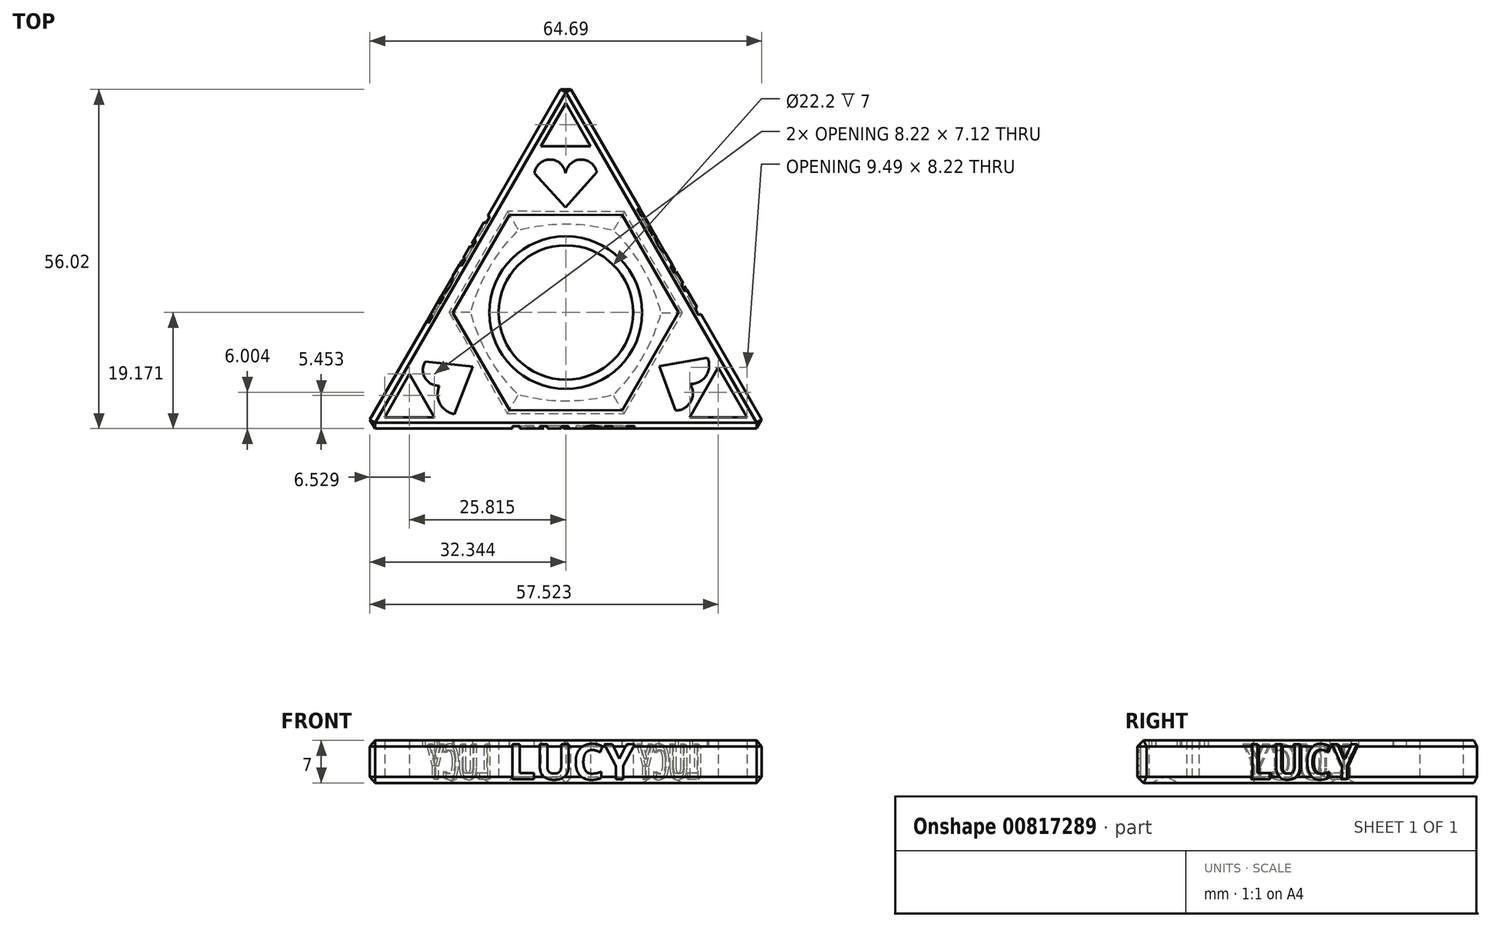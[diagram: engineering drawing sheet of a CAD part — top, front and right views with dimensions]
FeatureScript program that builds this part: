
annotation { "Feature Type Name" : "Feature", "Feature Type Description" : "" }
export const myFeature = defineFeature(function(context is Context, id is Id, definition is map)
    precondition{}
    {
        {
            var Q0;
            Q0=qCreatedBy(makeId("Top.planeOp"),FACE);
            var sketch = newSketch(context, id + "F0", { "sketchPlane" : qUnion([Q0])});
            skLineSegment(sketch, "E0.top", {"start": v(-48.66, -50.6) * mm, "end": v(17.76, -50.6) * mm});
            skLineSegment(sketch, "E1", {"start": v(-48.66, -50.6) * mm, "end": v(-15.45, 6.92) * mm});
            skLineSegment(sketch, "E2", {"start": v(-15.45, 6.92) * mm, "end": v(17.76, -50.6) * mm});
            skCircle(sketch, "E3", {"center": v(-15.45, -31.43) * mm, "radius": 11.1 * mm});
            skPoint(sketch, "E4.start.orphan", {"position": v(-32.05, -21.84) * mm});
            skPoint(sketch, "E5.trimOffspring.end.orphan", {"position": v(-15.45, -50.6) * mm});
            skPoint(sketch, "E6.trimOffspring.end.orphan", {"position": v(0, -21.31) * mm});
            skLineSegment(sketch, "E7.0", {"start": v(-45.37, -48.7) * mm, "end": v(-41.26, -41.59) * mm});
            skLineSegment(sketch, "E8.0", {"start": v(-15.45, 3.12) * mm, "end": v(-11.34, -4) * mm});
            skLineSegment(sketch, "E9.0", {"start": v(-45.37, -48.7) * mm, "end": v(-37.15, -48.7) * mm});
            skLineSegment(sketch, "E10", {"start": v(-37.15, -48.7) * mm, "end": v(-41.26, -41.59) * mm});
            skLineSegment(sketch, "E11", {"start": v(-15.45, -4) * mm, "end": v(-11.34, -4) * mm});
            skLineSegment(sketch, "E12", {"start": v(-15.45, -4) * mm, "end": v(-19.55, -4) * mm});
            skLineSegment(sketch, "E13", {"start": v(7.36, -44.6) * mm, "end": v(9.73, -40.49) * mm});
            skLineSegment(sketch, "E14", {"start": v(7.36, -44.6) * mm, "end": v(4.99, -48.7) * mm});
            skLineSegment(sketch, "E15.trimOffspring", {"start": v(4.99, -48.7) * mm, "end": v(14.48, -48.7) * mm});
            skLineSegment(sketch, "E16.trimOffspring", {"start": v(-19.55, -4) * mm, "end": v(-15.45, 3.12) * mm});
            skLineSegment(sketch, "E17.trimOffspring", {"start": v(9.73, -40.49) * mm, "end": v(14.48, -48.7) * mm});
            skSolve(sketch);
        }
        {
            var Q0;
            Q0=makeQuery(id+"F0.imprint","IMPRINT",FACE,{"disambiguationData":[TD([[makeQuery(id+"F0.imprint","IMPRINT",EDGE,{"derivedFrom":sQuery(id+"F0.wireOp",EDGE,"E0.top")}),1.0]])]});
            extrude(context, id + "F1", {"entities" : qUnion([Q0]), "depth" : 7 * mm, "offsetDistance" : 25 * mm});
        }
        {
            var Q0;
            Q0=makeQuery(id+"F1.opExtrude","SWEPT_FACE",FACE,{"disambiguationData":[OSD([sQuery(id+"F0.wireOp",EDGE,"E0.top")])]});
            var Q1;
            Q1=makeQuery(id+"F1.opExtrude","SWEPT_FACE",FACE,{"disambiguationData":[OSD([sQuery(id+"F0.wireOp",EDGE,"E2")])]});
            var Q2;
            Q2=makeQuery(id+"F1.opExtrude","SWEPT_FACE",FACE,{"disambiguationData":[OSD([sQuery(id+"F0.wireOp",EDGE,"E1")])]});
            chamfer(context, id + "F2", {"entities" : qUnion([Q0, Q1, Q2]), "width" : 1 * mm, "tangentPropagation" : true});
        }
        {
            var Q0;
            Q0=makeQuery(id+"F1.opExtrude","CAP_FACE",FACE,{"disambiguationData":[OSD([sQuery(id+"F0.wireOp",EDGE,"E0.top"),sQuery(id+"F0.wireOp",EDGE,"E1"),sQuery(id+"F0.wireOp",EDGE,"E2"),sQuery(id+"F0.wireOp",EDGE,"E3"),sQuery(id+"F0.wireOp",EDGE,"E7.0"),sQuery(id+"F0.wireOp",EDGE,"E8.0"),sQuery(id+"F0.wireOp",EDGE,"E9.0"),sQuery(id+"F0.wireOp",EDGE,"E10"),sQuery(id+"F0.wireOp",EDGE,"E11"),sQuery(id+"F0.wireOp",EDGE,"E12"),sQuery(id+"F0.wireOp",EDGE,"E13"),sQuery(id+"F0.wireOp",EDGE,"E14"),sQuery(id+"F0.wireOp",EDGE,"E15.trimOffspring"),sQuery(id+"F0.wireOp",EDGE,"E16.trimOffspring"),sQuery(id+"F0.wireOp",EDGE,"E17.trimOffspring")])],"isStart":false});
            var sketch = newSketch(context, id + "F3", { "sketchPlane" : qUnion([Q0])});
            skCircle(sketch, "E18.0", {"center": v(-15.45, -31.43) * mm, "radius": 12.6 * mm});
            skCircle(sketch, "E19.cCircle", {"center": v(-15.45, -31.43) * mm, "radius": 18.63 * mm, "construction": true});
            skLineSegment(sketch, "E19.0", {"start": v(-6.16, -15.28) * mm, "end": v(3.18, -31.4) * mm});
            skLineSegment(sketch, "E19.1", {"start": v(3.18, -31.4) * mm, "end": v(-6.1, -47.54) * mm});
            skLineSegment(sketch, "E19.2", {"start": v(-6.1, -47.54) * mm, "end": v(-24.73, -47.58) * mm});
            skLineSegment(sketch, "E19.3", {"start": v(-24.73, -47.58) * mm, "end": v(-34.08, -31.47) * mm});
            skLineSegment(sketch, "E19.4", {"start": v(-34.08, -31.47) * mm, "end": v(-24.8, -15.31) * mm});
            skLineSegment(sketch, "E19.5", {"start": v(-24.8, -15.31) * mm, "end": v(-6.16, -15.28) * mm});
            skSolve(sketch);
        }
        {
            var Q0;
            Q0=makeQuery(id+"F3.imprint","IMPRINT",FACE,{"disambiguationData":[TD([[makeQuery(id+"F3.imprint","IMPRINT",EDGE,{"derivedFrom":sQuery(id+"F3.wireOp",EDGE,"E18.0")}),-1.0]])]});
            extrude(context, id + "F4", {"entities" : qUnion([Q0]), "operationType" : NewBodyOperationType.REMOVE, "oppositeDirection" : true, "depth" : 1 * mm, "offsetDistance" : 25 * mm});
        }
        {
            var Q0;
            Q0=makeQuery(id+"F1.opExtrude","CAP_FACE",FACE,{"disambiguationData":[OSD([sQuery(id+"F0.wireOp",EDGE,"E0.top"),sQuery(id+"F0.wireOp",EDGE,"E1"),sQuery(id+"F0.wireOp",EDGE,"E2"),sQuery(id+"F0.wireOp",EDGE,"E3"),sQuery(id+"F0.wireOp",EDGE,"E7.0"),sQuery(id+"F0.wireOp",EDGE,"E8.0"),sQuery(id+"F0.wireOp",EDGE,"E9.0"),sQuery(id+"F0.wireOp",EDGE,"E10"),sQuery(id+"F0.wireOp",EDGE,"E11"),sQuery(id+"F0.wireOp",EDGE,"E12"),sQuery(id+"F0.wireOp",EDGE,"E13"),sQuery(id+"F0.wireOp",EDGE,"E14"),sQuery(id+"F0.wireOp",EDGE,"E15.trimOffspring"),sQuery(id+"F0.wireOp",EDGE,"E16.trimOffspring"),sQuery(id+"F0.wireOp",EDGE,"E17.trimOffspring")])],"isStart":true});
            var sketch = newSketch(context, id + "F5", { "sketchPlane" : qUnion([Q0])});
            skCircle(sketch, "E20.0", {"center": v(-15.45, 31.43) * mm, "radius": 12.6 * mm});
            skCircle(sketch, "E21.cCircle", {"center": v(-15.45, 31.43) * mm, "radius": 19.26 * mm, "construction": true});
            skLineSegment(sketch, "E21.0", {"start": v(-5.86, 48.14) * mm, "end": v(3.82, 31.48) * mm});
            skLineSegment(sketch, "E21.1", {"start": v(3.82, 31.48) * mm, "end": v(-5.77, 14.77) * mm});
            skLineSegment(sketch, "E21.2", {"start": v(-5.77, 14.77) * mm, "end": v(-25.04, 14.72) * mm});
            skLineSegment(sketch, "E21.3", {"start": v(-25.04, 14.72) * mm, "end": v(-34.7, 31.38) * mm});
            skLineSegment(sketch, "E21.4", {"start": v(-34.7, 31.38) * mm, "end": v(-25.12, 48.09) * mm});
            skLineSegment(sketch, "E21.5", {"start": v(-25.12, 48.09) * mm, "end": v(-5.86, 48.14) * mm});
            skSolve(sketch);
        }
        {
            var Q0;
            Q0=makeQuery(id+"F5.imprint","IMPRINT",FACE,{"disambiguationData":[TD([[makeQuery(id+"F5.imprint","IMPRINT",EDGE,{"derivedFrom":sQuery(id+"F5.wireOp",EDGE,"E20.0")}),-1.0]])]});
            extrude(context, id + "F6", {"entities" : qUnion([Q0]), "operationType" : NewBodyOperationType.REMOVE, "oppositeDirection" : true, "depth" : 1 * mm, "offsetDistance" : 25 * mm});
        }
        {
            var Q0;
            Q0=makeQuery(id+"F6.boolean.opBoolean","COPY",FACE,{"derivedFrom":makeQuery(id+"F6.opExtrude","CAP_FACE",FACE,{"disambiguationData":[OSD([sQuery(id+"F5.wireOp",EDGE,"E20.0"),sQuery(id+"F5.wireOp",EDGE,"E21.0"),sQuery(id+"F5.wireOp",EDGE,"E21.1"),sQuery(id+"F5.wireOp",EDGE,"E21.2"),sQuery(id+"F5.wireOp",EDGE,"E21.3"),sQuery(id+"F5.wireOp",EDGE,"E21.4"),sQuery(id+"F5.wireOp",EDGE,"E21.5")])],"isStart":false})});
            fillet(context, id + "F7", {"entities" : qUnion([Q0]), "radius" : 5 * mm, "tangentPropagation" : true, "allowEdgeOverflow" : false});
        }
        {
            var Q0;
            Q0=makeQuery(id+"F1.opExtrude","SWEPT_FACE",FACE,{"disambiguationData":[OSD([sQuery(id+"F0.wireOp",EDGE,"E2")])]});
            var sketch = newSketch(context, id + "F8", { "sketchPlane" : qUnion([Q0])});
            skText(sketch, "E22", { "text": "LUCY", "fontName": "OpenSans-Bold.ttf"});
            const initialGuessF8  = {"E22": [-0.03156, 0.00058, 1, 0, 0.00585]};
            skSetInitialGuess(sketch, initialGuessF8);
            skSolve(sketch);
        }
        {
            var Q0;
            Q0 = qSketchRegion(id + "F8", true);
            extrude(context, id + "F9", {"entities" : qUnion([Q0]), "operationType" : NewBodyOperationType.REMOVE, "oppositeDirection" : true, "depth" : 0.5 * mm, "offsetDistance" : 25 * mm});
        }
        {
            var Q0;
            Q0=makeQuery(id+"F1.opExtrude","SWEPT_FACE",FACE,{"disambiguationData":[OSD([sQuery(id+"F0.wireOp",EDGE,"E1")])]});
            var sketch = newSketch(context, id + "F10", { "sketchPlane" : qUnion([Q0])});
            skText(sketch, "E23", { "text": "LUCY", "fontName": "OpenSans-Bold.ttf"});
            const initialGuessF10  = {"E23": [0.02681, 0.00058, 1, 0, 0.00585]};
            skSetInitialGuess(sketch, initialGuessF10);
            skSolve(sketch);
        }
        {
            var Q0;
            Q0 = qSketchRegion(id + "F10", true);
            extrude(context, id + "F11", {"entities" : qUnion([Q0]), "operationType" : NewBodyOperationType.REMOVE, "oppositeDirection" : true, "depth" : 0.5 * mm, "offsetDistance" : 25 * mm});
        }
        {
            var Q0;
            Q0=makeQuery(id+"F1.opExtrude","SWEPT_FACE",FACE,{"disambiguationData":[OSD([sQuery(id+"F0.wireOp",EDGE,"E0.top")])]});
            var sketch = newSketch(context, id + "F12", { "sketchPlane" : qUnion([Q0])});
            skText(sketch, "E24", { "text": "LUCY", "fontName": "OpenSans-Bold.ttf"});
            const initialGuessF12  = {"E24": [-0.02502, 0.00058, 1, 0, 0.00585]};
            skSetInitialGuess(sketch, initialGuessF12);
            skSolve(sketch);
        }
        {
            var Q0;
            Q0 = qSketchRegion(id + "F12", true);
            extrude(context, id + "F13", {"entities" : qUnion([Q0]), "operationType" : NewBodyOperationType.REMOVE, "oppositeDirection" : true, "depth" : 0.5 * mm, "offsetDistance" : 25 * mm});
        }
        {
            var Q0;
            {var subQ0=sQuery(id+"F0.wireOp",EDGE,"E1");var subQ1=sQuery(id+"F0.wireOp",EDGE,"E0.top");var subQ2=sQuery(id+"F0.wireOp",EDGE,"E12");var subQ3=sQuery(id+"F0.wireOp",EDGE,"E11");var subQ4=sQuery(id+"F0.wireOp",EDGE,"E17.trimOffspring");var subQ5=sQuery(id+"F0.wireOp",EDGE,"E2");var subQ6=sQuery(id+"F0.wireOp",EDGE,"E16.trimOffspring");var subQ7=sQuery(id+"F0.wireOp",EDGE,"E15.trimOffspring");var subQ8=sQuery(id+"F0.wireOp",EDGE,"E14");var subQ9=sQuery(id+"F0.wireOp",EDGE,"E13");var subQ10=sQuery(id+"F0.wireOp",EDGE,"E7.0");var subQ11=sQuery(id+"F0.wireOp",EDGE,"E8.0");var subQ12=sQuery(id+"F0.wireOp",EDGE,"E9.0");var subQ13=sQuery(id+"F0.wireOp",EDGE,"E10");Q0=makeQuery(id+"F4.boolean.opBoolean","SPLIT",FACE,{"disambiguationData":[TD([makeQuery(id+"F1.opExtrude","SWEPT_FACE",FACE,{"disambiguationData":[OSD([subQ10])]})])],"derivedFrom":makeQuery(id+"F1.opExtrude","CAP_FACE",FACE,{"disambiguationData":[OSD([subQ1,subQ0,subQ5,sQuery(id+"F0.wireOp",EDGE,"E3"),subQ10,subQ11,subQ12,subQ13,subQ3,subQ2,subQ9,subQ8,subQ7,subQ6,subQ4])],"isStart":false})});}
            var sketch = newSketch(context, id + "F14", { "sketchPlane" : qUnion([Q0])});
            skArc(sketch, "E25", {"start": v(-10.32, -8.3) * mm, "mid": v(-12.95, -6.17) * mm, "end": v(-15.5, -8.39) * mm});
            skArc(sketch, "E26", {"start": v(-15.5, -8.39) * mm, "mid": v(-18.06, -6.18) * mm, "end": v(-20.62, -8.39) * mm});
            skLineSegment(sketch, "E27", {"start": v(-20.62, -8.39) * mm, "end": v(-15.48, -14.07) * mm});
            skLineSegment(sketch, "E28", {"start": v(-15.48, -14.07) * mm, "end": v(-10.32, -8.3) * mm});
            skArc(sketch, "E29", {"start": v(-36.3, -43.5) * mm, "mid": v(-36.24, -46.46) * mm, "end": v(-33.86, -48.2) * mm});
            skArc(sketch, "E30", {"start": v(-38.62, -39.5) * mm, "mid": v(-38.7, -42.23) * mm, "end": v(-36.3, -43.5) * mm});
            skLineSegment(sketch, "E31", {"start": v(-38.62, -39.5) * mm, "end": v(-30.79, -40.32) * mm});
            skLineSegment(sketch, "E32", {"start": v(-33.86, -48.2) * mm, "end": v(-30.79, -40.32) * mm});
            skArc(sketch, "E33", {"start": v(2.68, -47.6) * mm, "mid": v(5.18, -46.14) * mm, "end": v(5.09, -43.25) * mm});
            skArc(sketch, "E34", {"start": v(5.09, -43.25) * mm, "mid": v(7.73, -41.85) * mm, "end": v(7.91, -38.87) * mm});
            skLineSegment(sketch, "E35", {"start": v(7.91, -38.87) * mm, "end": v(0, -40.3) * mm});
            skLineSegment(sketch, "E36", {"start": v(0, -40.3) * mm, "end": v(2.68, -47.6) * mm});
            skSolve(sketch);
        }
        {
            var Q0;
            Q0=makeQuery(id+"F14.imprint","IMPRINT",FACE,{"disambiguationData":[TD([[makeQuery(id+"F14.imprint","IMPRINT",EDGE,{"derivedFrom":sQuery(id+"F14.wireOp",EDGE,"E33")}),1.0]])]});
            var Q1;
            Q1=makeQuery(id+"F14.imprint","IMPRINT",FACE,{"disambiguationData":[TD([[makeQuery(id+"F14.imprint","IMPRINT",EDGE,{"derivedFrom":sQuery(id+"F14.wireOp",EDGE,"E25")}),1.0]])]});
            var Q2;
            Q2=makeQuery(id+"F14.imprint","IMPRINT",FACE,{"disambiguationData":[TD([[makeQuery(id+"F14.imprint","IMPRINT",EDGE,{"derivedFrom":sQuery(id+"F14.wireOp",EDGE,"E29")}),1.0]])]});
            var Q3;
            Q3=makeQuery(id+"F4.boolean.opBoolean","COPY",FACE,{"derivedFrom":makeQuery(id+"F4.opExtrude","CAP_FACE",FACE,{"disambiguationData":[OSD([sQuery(id+"F3.wireOp",EDGE,"E18.0"),sQuery(id+"F3.wireOp",EDGE,"E19.0"),sQuery(id+"F3.wireOp",EDGE,"E19.1"),sQuery(id+"F3.wireOp",EDGE,"E19.2"),sQuery(id+"F3.wireOp",EDGE,"E19.3"),sQuery(id+"F3.wireOp",EDGE,"E19.4"),sQuery(id+"F3.wireOp",EDGE,"E19.5")])],"isStart":false})});
            extrude(context, id + "F15", {"entities" : qUnion([Q0, Q1, Q2]), "operationType" : NewBodyOperationType.REMOVE, "endBound" : BoundingType.UP_TO_SURFACE, "oppositeDirection" : true, "depth" : 25 * mm, "endBoundEntityFace" : qUnion([Q3]), "offsetDistance" : 25 * mm});
        }
    });
